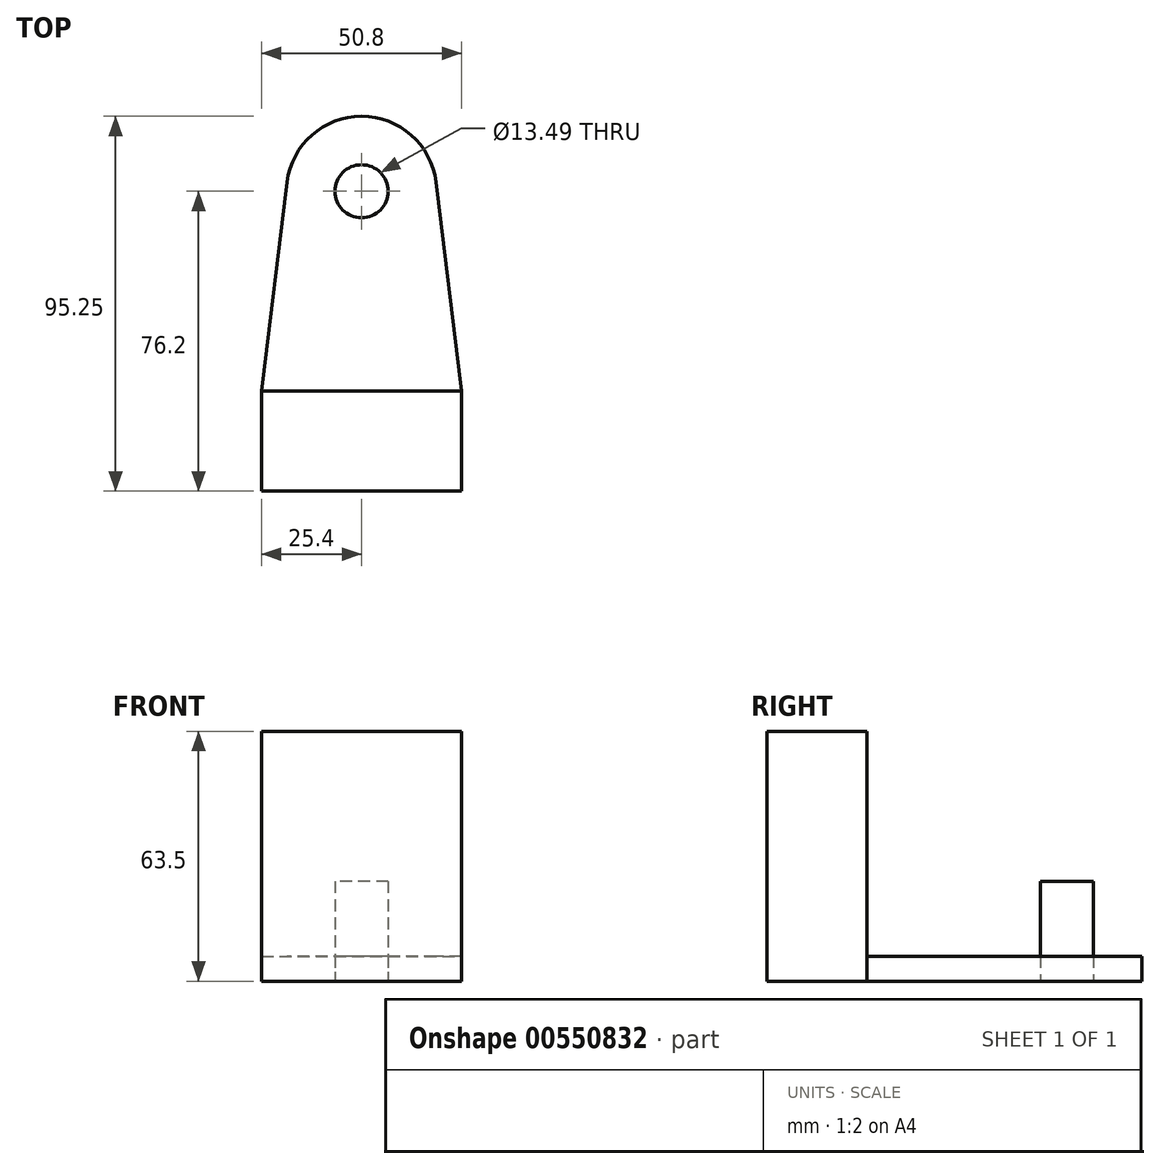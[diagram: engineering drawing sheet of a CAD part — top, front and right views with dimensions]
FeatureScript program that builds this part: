
annotation { "Feature Type Name" : "Feature", "Feature Type Description" : "" }
export const myFeature = defineFeature(function(context is Context, id is Id, definition is map)
    precondition{}
    {
        {
            var Q0;
            Q0=qCreatedBy(makeId("Top.planeOp"),FACE);
            var sketch = newSketch(context, id + "F0", { "sketchPlane" : qUnion([Q0])});
            skCircle(sketch, "E0", {"center": v(0, 0) * mm, "radius": 6.74 * mm});
            skArc(sketch, "E1", {"start": v(18.9, 2.31) * mm, "mid": v(0, 19.05) * mm, "end": v(-18.9, 2.31) * mm});
            skLineSegment(sketch, "E2", {"start": v(0, 0) * mm, "end": v(0, -50.8) * mm, "construction": true});
            skLineSegment(sketch, "E3", {"start": v(-25.4, -50.8) * mm, "end": v(25.4, -50.8) * mm});
            skLineSegment(sketch, "E4", {"start": v(-25.4, -50.8) * mm, "end": v(-18.9, 2.31) * mm});
            skLineSegment(sketch, "E5", {"start": v(25.4, -50.8) * mm, "end": v(18.9, 2.31) * mm});
            skSolve(sketch);
        }
        {
            var Q0;
            Q0 = qSketchRegion(id + "F0", true);
            extrude(context, id + "F1", {"entities" : qUnion([Q0]), "depth" : 6.35 * mm, "offsetDistance" : 25.4 * mm});
        }
        {
            var Q0;
            Q0=makeQuery(id+"F1.opExtrude","SWEPT_FACE",FACE,{"disambiguationData":[OSD([sQuery(id+"F0.wireOp",EDGE,"E3")])]});
            var sketch = newSketch(context, id + "F2", { "sketchPlane" : qUnion([Q0])});
            skLineSegment(sketch, "E6.top", {"start": v(-25.4, 63.5) * mm, "end": v(25.4, 63.5) * mm});
            skLineSegment(sketch, "E6.left", {"start": v(-25.4, 0) * mm, "end": v(-25.4, 63.5) * mm});
            skLineSegment(sketch, "E6.right", {"start": v(25.4, 0) * mm, "end": v(25.4, 63.5) * mm});
            skSolve(sketch);
        }
        {
            var Q0;
            {var subQ0=sQuery(id+"F2.wireOp",EDGE,"E6.top");Q0=makeQuery(id+"F2.imprint","IMPRINT",FACE,{"disambiguationData":[TD([[makeQuery(id+"F2.imprint","IMPRINT",EDGE,{"derivedFrom":subQ0}),-1.0]])]});}
            var Q1;
            {var subQ1=sQuery(id+"F0.wireOp",EDGE,"E3");var subQ2=makeQuery(id+"F1.opExtrude","CAP_EDGE",EDGE,{"disambiguationData":[OSD([subQ1])],"isStart":true});Q1=makeQuery(id+"F2.imprint","IMPRINT",FACE,{"disambiguationData":[TD([[makeQuery(id+"F2.imprint","IMPRINT",EDGE,{"derivedFrom":subQ2}),1.0]])]});}
            extrude(context, id + "F3", {"entities" : qUnion([Q0, Q1]), "depth" : 25.4 * mm, "offsetDistance" : 25.4 * mm});
        }
        {
            var Q0;
            Q0=makeQuery(id+"F1.opExtrude","CAP_FACE",FACE,{"disambiguationData":[OSD([sQuery(id+"F0.wireOp",EDGE,"E0"),sQuery(id+"F0.wireOp",EDGE,"E1"),sQuery(id+"F0.wireOp",EDGE,"E3"),sQuery(id+"F0.wireOp",EDGE,"E4"),sQuery(id+"F0.wireOp",EDGE,"E5")])],"isStart":true});
            var sketch = newSketch(context, id + "F4", { "sketchPlane" : qUnion([Q0])});
            skCircle(sketch, "E7", {"center": v(0, 0) * mm, "radius": 6.74 * mm});
            skSolve(sketch);
        }
        {
            var Q0;
            Q0 = qSketchRegion(id + "F4", true);
            extrude(context, id + "F5", {"entities" : qUnion([Q0]), "oppositeDirection" : true, "depth" : 25.4 * mm, "offsetDistance" : 25.4 * mm});
        }
    });
